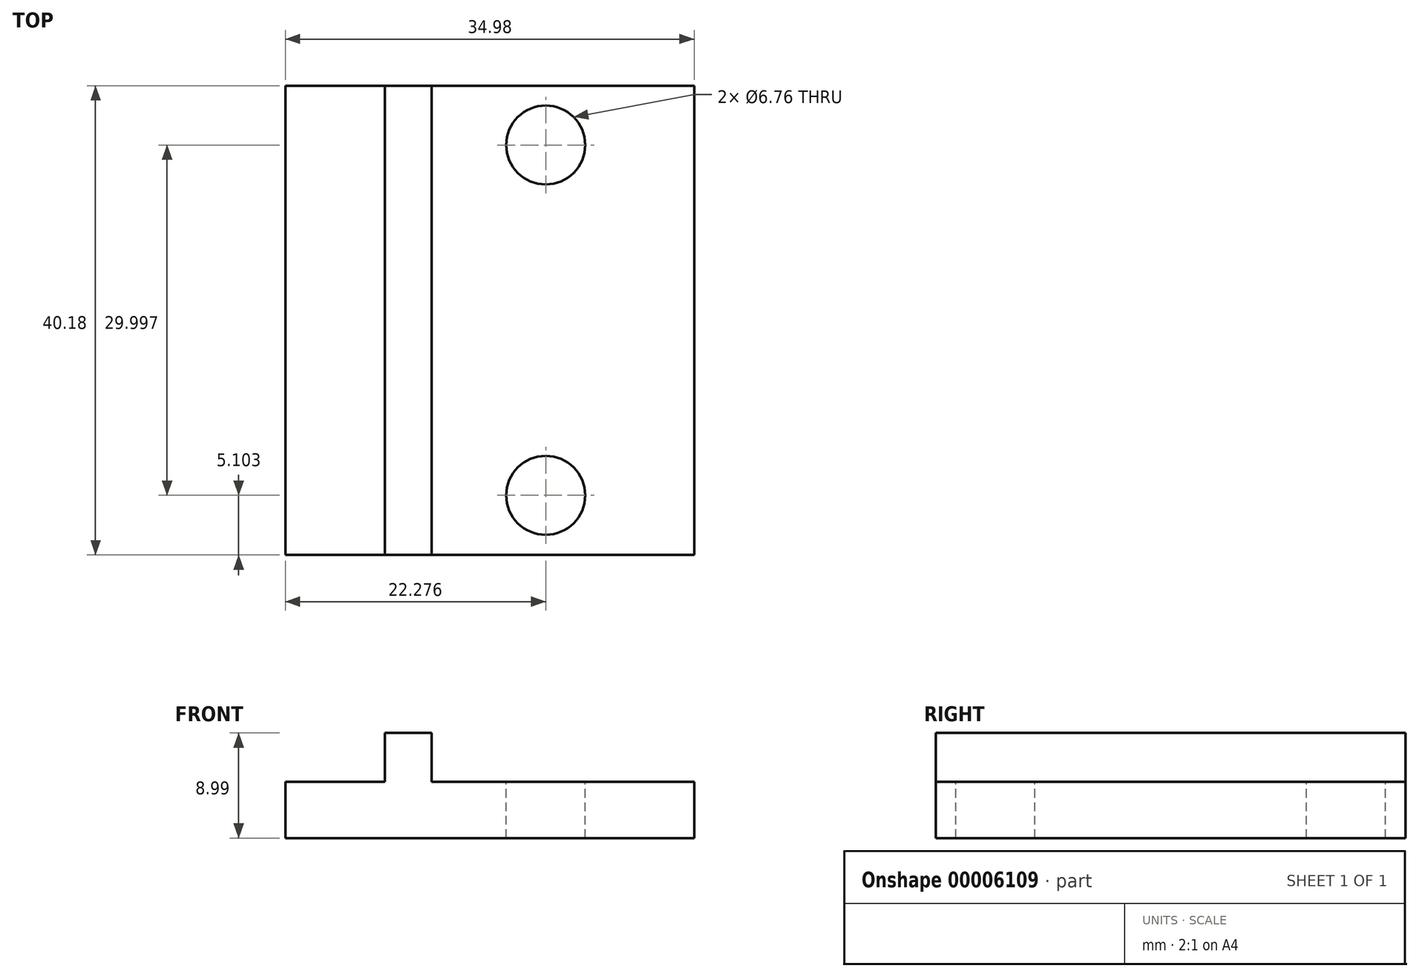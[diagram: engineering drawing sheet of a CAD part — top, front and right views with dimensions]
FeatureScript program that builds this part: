
annotation { "Feature Type Name" : "Feature", "Feature Type Description" : "" }
export const myFeature = defineFeature(function(context is Context, id is Id, definition is map)
    precondition{}
    {
        {
            var Q0;
            Q0=qCreatedBy(makeId("Front.planeOp"),FACE);
            var sketch = newSketch(context, id + "F0", { "sketchPlane" : qUnion([Q0])});
            skLineSegment(sketch, "E0", {"start": v(0, -9) * mm, "end": v(0, -4.17) * mm});
            skLineSegment(sketch, "E1.0.MirrorCS", {"start": v(8.5, 0) * mm, "end": v(12.5, 0) * mm});
            skLineSegment(sketch, "E1.1.MirrorCS", {"start": v(12.5, 0) * mm, "end": v(12.5, -4.17) * mm});
            skLineSegment(sketch, "E1.2.MirrorCS", {"start": v(12.5, -4.17) * mm, "end": v(34.98, -4.17) * mm});
            skLineSegment(sketch, "E1.3.MirrorCS", {"start": v(34.98, -9) * mm, "end": v(0, -9) * mm});
            skLineSegment(sketch, "E1.4.MirrorCS", {"start": v(34.98, -4.17) * mm, "end": v(34.98, -9) * mm});
            skLineSegment(sketch, "E1.5.MirrorCS", {"start": v(8.5, -4.17) * mm, "end": v(8.5, 0) * mm});
            skLineSegment(sketch, "E1.6.MirrorCS", {"start": v(0, -4.17) * mm, "end": v(8.5, -4.17) * mm});
            skSolve(sketch);
        }
        {
            var Q0;
            Q0 = qSketchRegion(id + "F0", true);
            extrude(context, id + "F1", {"entities" : qUnion([Q0]), "depth" : 40.18 * mm});
        }
        {
            var Q0;
            Q0=makeQuery(id+"F1.opExtrude","SWEPT_FACE",FACE,{"disambiguationData":[OSD([sQuery(id+"F0.wireOp",EDGE,"E1.2.MirrorCS")])]});
            var sketch = newSketch(context, id + "F2", { "sketchPlane" : qUnion([Q0])});
            skCircle(sketch, "E2", {"center": v(22.28, -5.08) * mm, "radius": 3.38 * mm});
            skCircle(sketch, "E3", {"center": v(22.28, -35.08) * mm, "radius": 3.38 * mm});
            skSolve(sketch);
        }
        {
            var Q0;
            Q0 = qSketchRegion(id + "F2", true);
            extrude(context, id + "F3", {"entities" : qUnion([Q0]), "operationType" : NewBodyOperationType.REMOVE, "endBound" : BoundingType.THROUGH_ALL, "oppositeDirection" : true, "depth" : 25.4 * mm});
        }
    });
